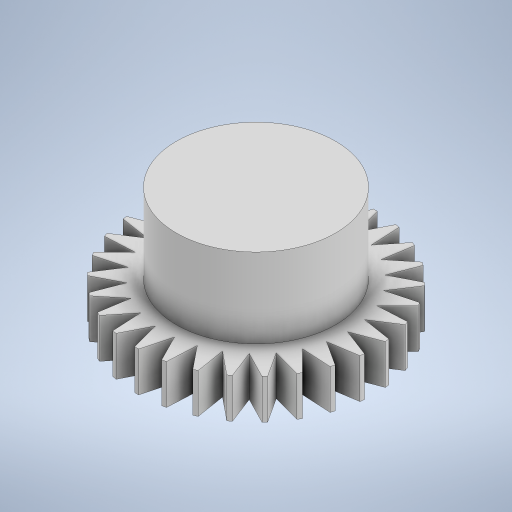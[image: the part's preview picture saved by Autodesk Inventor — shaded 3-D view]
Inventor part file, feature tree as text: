
AUTODESK INVENTOR PART (.ipt)
format: ipt  version: 2024 (Build 280153000, 153)  size: 375,296 bytes
history: native  units: mm
features: extrude x3, sketch x3
ambient origin geometry x8: Origin, YZ Plane, XZ Plane, XY Plane, X Axis, Y Axis, Z Axis, Center Point
bodies: Solid1 (feature_tree)
feature tree (6):
  extrude  "Extrusion1"  Depth=300.0mm TaperAngle=360.0deg
  extrude  "Extrusion2"  Depth=3.0mm
  extrude  "Extrusion3"  Depth=3.0mm TaperAngle=0.0deg
  sketch  "Sketch1"  dims[d0=30.0mm d1=300.0mm d3=360.0deg]
  sketch  "Sketch2"  dims[d5=5.0mm d6=0.0mm d7=3.0mm]
  sketch  "Sketch3"  dims[d8=15.0mm d9=3.0mm d10=0.0mm d11=20.0mm d12=10.0mm d13=0.0mm]
